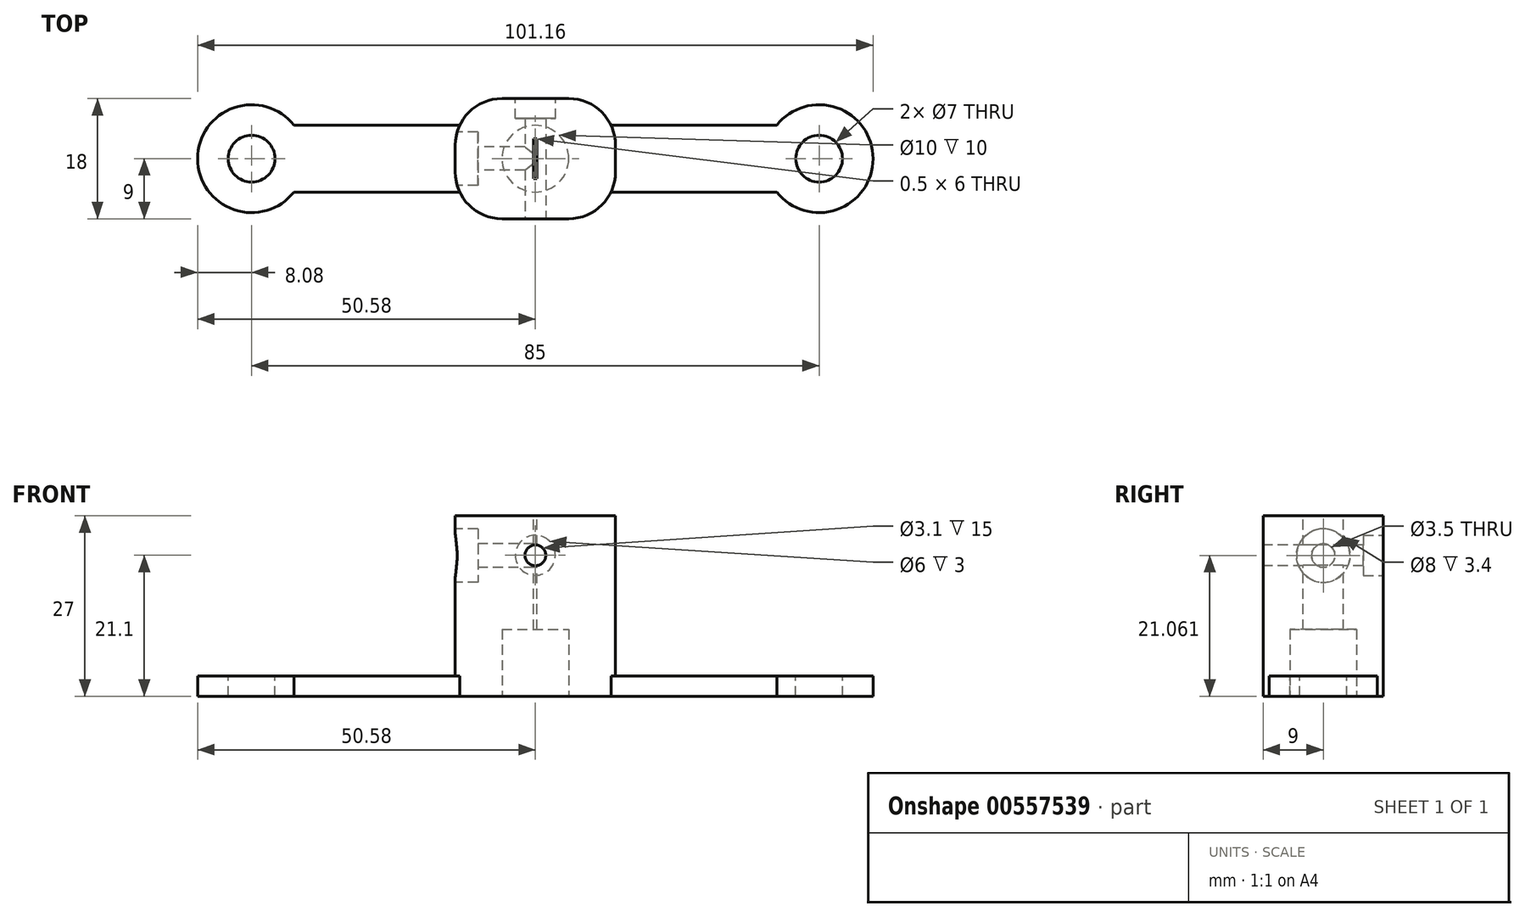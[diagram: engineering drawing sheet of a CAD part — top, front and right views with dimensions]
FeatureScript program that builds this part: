
annotation { "Feature Type Name" : "Feature", "Feature Type Description" : "" }
export const myFeature = defineFeature(function(context is Context, id is Id, definition is map)
    precondition{}
    {
        {
            var Q0;
            Q0=qCreatedBy(makeId("Top.planeOp"),FACE);
            var sketch = newSketch(context, id + "F0", { "sketchPlane" : qUnion([Q0])});
            skLineSegment(sketch, "E0.bottom", {"start": v(42.5, -5) * mm, "end": v(-42.5, -5) * mm});
            skLineSegment(sketch, "E0.top", {"start": v(42.5, 5) * mm, "end": v(-42.5, 5) * mm});
            skLineSegment(sketch, "E0.left", {"start": v(42.5, -5) * mm, "end": v(42.5, 5) * mm});
            skLineSegment(sketch, "E0.right", {"start": v(-42.5, -5) * mm, "end": v(-42.5, 5) * mm});
            skPoint(sketch, "E0.middle", {"position": v(0, 0) * mm});
            skCircle(sketch, "E1", {"center": v(-42.5, 0) * mm, "radius": 8.08 * mm});
            skCircle(sketch, "E2.MirrorC", {"center": v(42.5, 0) * mm, "radius": 8.08 * mm});
            skSolve(sketch);
        }
        {
            var Q0;
            {var subQ0=sQuery(id+"F0.wireOp",EDGE,"E0.left");Q0=makeQuery(id+"F0.imprint","IMPRINT",FACE,{"disambiguationData":[TD([[makeQuery(id+"F0.imprint","IMPRINT",EDGE,{"derivedFrom":subQ0}),-1.0]])]});}
            var Q1;
            {var subQ0=sQuery(id+"F0.wireOp",EDGE,"E0.right");Q1=makeQuery(id+"F0.imprint","IMPRINT",FACE,{"disambiguationData":[TD([[makeQuery(id+"F0.imprint","IMPRINT",EDGE,{"derivedFrom":subQ0}),1.0]])]});}
            var Q2;
            {var subQ0=sQuery(id+"F0.wireOp",EDGE,"E0.left");Q2=makeQuery(id+"F0.imprint","IMPRINT",FACE,{"disambiguationData":[TD([[makeQuery(id+"F0.imprint","IMPRINT",EDGE,{"derivedFrom":subQ0}),1.0]])]});}
            var Q3;
            {var subQ0=sQuery(id+"F0.wireOp",EDGE,"E2.MirrorC");var subQ1=sQuery(id+"F0.wireOp",EDGE,"E0.bottom");var subQ2=makeQuery(id+"F0.imprint","INTERSECT",VERTEX,{"derivedFrom":[subQ1,subQ0]});Q3=makeQuery(id+"F0.imprint","IMPRINT",FACE,{"disambiguationData":[TD([[makeQuery(id+"F0.imprint","IMPRINT",EDGE,{"disambiguationData":[TD([[subQ2,-1.0]])],"derivedFrom":subQ1}),-1.0]])]});}
            var Q4;
            {var subQ0=sQuery(id+"F0.wireOp",EDGE,"E0.right");Q4=makeQuery(id+"F0.imprint","IMPRINT",FACE,{"disambiguationData":[TD([[makeQuery(id+"F0.imprint","IMPRINT",EDGE,{"derivedFrom":subQ0}),-1.0]])]});}
            extrude(context, id + "F1", {"entities" : qUnion([Q0, Q1, Q2, Q3, Q4]), "depth" : 3 * mm, "offsetDistance" : 25 * mm});
        }
        {
            var Q0;
            Q0=makeQuery(id+"F1.opExtrude","CAP_FACE",FACE,{"disambiguationData":[OSD([sQuery(id+"F0.wireOp",EDGE,"E0.bottom"),sQuery(id+"F0.wireOp",EDGE,"E0.top"),sQuery(id+"F0.wireOp",EDGE,"E1"),sQuery(id+"F0.wireOp",EDGE,"E2.MirrorC")])],"isStart":false});
            var sketch = newSketch(context, id + "F2", { "sketchPlane" : qUnion([Q0])});
            skCircle(sketch, "E3", {"center": v(-42.5, 0) * mm, "radius": 3.05 * mm});
            skCircle(sketch, "E4.MirrorC", {"center": v(42.5, 0) * mm, "radius": 3.05 * mm});
            skSolve(sketch);
        }
        {
            var Q0;
            Q0=sQuery(id+"F2.wireOp",VERTEX,"E3.center");
            var Q1;
            Q1=sQuery(id+"F2.wireOp",VERTEX,"E4.MirrorC.center");
            var Q2;
            Q2=makeQuery(id+"F1.opExtrude","SWEPT_BODY",BODY,{"disambiguationData":[OSD([sQuery(id+"F0.wireOp",EDGE,"E0.bottom"),sQuery(id+"F0.wireOp",EDGE,"E0.top"),sQuery(id+"F0.wireOp",EDGE,"E1"),sQuery(id+"F0.wireOp",EDGE,"E2.MirrorC")])]});
            hole(context, id + "F3", {"style" : HoleStyle.SIMPLE, "endStyle" : HoleEndStyle.THROUGH, "holeDiameter" : 7 * mm, "isTappedThrough" : true, "tappedDepth" : 12 * mm, "tapClearance" : 3, "locations" : qUnion([Q0, Q1]), "scope" : qUnion([Q2])});
        }
        {
            var Q0;
            Q0=qCreatedBy(makeId("Top.planeOp"),FACE);
            var sketch = newSketch(context, id + "F4", { "sketchPlane" : qUnion([Q0])});
            skLineSegment(sketch, "E5.bottom", {"start": v(12, 9) * mm, "end": v(-12, 9) * mm});
            skLineSegment(sketch, "E5.top", {"start": v(12, -9) * mm, "end": v(-12, -9) * mm});
            skLineSegment(sketch, "E5.left", {"start": v(12, 9) * mm, "end": v(12, -9) * mm});
            skLineSegment(sketch, "E5.right", {"start": v(-12, 9) * mm, "end": v(-12, -9) * mm});
            skPoint(sketch, "E5.middle", {"position": v(0, 0) * mm});
            skSolve(sketch);
        }
        {
            var Q0;
            Q0=qSketchRegion(id+"F4",true);
            extrude(context, id + "F5", {"entities" : qUnion([Q0]), "operationType" : NewBodyOperationType.ADD, "depth" : 27 * mm, "offsetDistance" : 25 * mm});
        }
        {
            var Q0;
            Q0=qCreatedBy(makeId("Front.planeOp"),FACE);
            var sketch = newSketch(context, id + "F6", { "sketchPlane" : qUnion([Q0])});
            skCircle(sketch, "E6", {"center": v(0, 21.1) * mm, "radius": 1.55 * mm});
            skSolve(sketch);
        }
        {
            var Q0;
            Q0=qSketchRegion(id+"F6",true);
            extrude(context, id + "F7", {"entities" : qUnion([Q0]), "operationType" : NewBodyOperationType.REMOVE, "endBound" : BoundingType.SYMMETRIC, "oppositeDirection" : true, "depth" : 25 * mm, "offsetDistance" : 25 * mm});
        }
        {
            var Q0;
            Q0=makeQuery(id+"F5.opExtrude","SWEPT_FACE",FACE,{"disambiguationData":[OSD([sQuery(id+"F4.wireOp",EDGE,"E5.right")])]});
            var sketch = newSketch(context, id + "F8", { "sketchPlane" : qUnion([Q0])});
            skCircle(sketch, "E7", {"center": v(0, 21.06) * mm, "radius": 1.75 * mm});
            skSolve(sketch);
        }
        {
            var Q0;
            Q0=qSketchRegion(id+"F8",true);
            extrude(context, id + "F9", {"entities" : qUnion([Q0]), "operationType" : NewBodyOperationType.REMOVE, "oppositeDirection" : true, "depth" : 12 * mm, "offsetDistance" : 25 * mm});
        }
        {
            var Q0;
            Q0=makeQuery(id+"F5.opExtrude","SWEPT_FACE",FACE,{"disambiguationData":[OSD([sQuery(id+"F4.wireOp",EDGE,"E5.right")])]});
            var sketch = newSketch(context, id + "F10", { "sketchPlane" : qUnion([Q0])});
            skCircle(sketch, "E8", {"center": v(0, 21.06) * mm, "radius": 4 * mm});
            skSolve(sketch);
        }
        {
            var Q0;
            Q0=qSketchRegion(id+"F10",true);
            extrude(context, id + "F11", {"entities" : qUnion([Q0]), "operationType" : NewBodyOperationType.REMOVE, "oppositeDirection" : true, "depth" : 3.4 * mm, "offsetDistance" : 25 * mm});
        }
        {
            var Q0;
            Q0=makeQuery(id+"F5.opExtrude","SWEPT_EDGE",EDGE,{"disambiguationData":[OSD([sQuery(id+"F4.wireOp",EDGE,"E5.bottom"),sQuery(id+"F4.wireOp",EDGE,"E5.right")])]});
            fillet(context, id + "F12", {"entities" : qUnion([Q0]), "radius" : 7 * mm, "tangentPropagation" : true, "allowEdgeOverflow" : false});
        }
        {
            var Q0;
            Q0=makeQuery(id+"F5.opExtrude","SWEPT_EDGE",EDGE,{"disambiguationData":[OSD([sQuery(id+"F4.wireOp",EDGE,"E5.bottom"),sQuery(id+"F4.wireOp",EDGE,"E5.left")])]});
            fillet(context, id + "F13", {"entities" : qUnion([Q0]), "radius" : 7 * mm, "tangentPropagation" : true, "allowEdgeOverflow" : false});
        }
        {
            var Q0;
            Q0=makeQuery(id+"F5.opExtrude","SWEPT_EDGE",EDGE,{"disambiguationData":[OSD([sQuery(id+"F4.wireOp",EDGE,"E5.top"),sQuery(id+"F4.wireOp",EDGE,"E5.right")])]});
            fillet(context, id + "F14", {"entities" : qUnion([Q0]), "radius" : 7 * mm, "tangentPropagation" : true, "allowEdgeOverflow" : false});
        }
        {
            var Q0;
            Q0=makeQuery(id+"F5.opExtrude","SWEPT_EDGE",EDGE,{"disambiguationData":[OSD([sQuery(id+"F4.wireOp",EDGE,"E5.top"),sQuery(id+"F4.wireOp",EDGE,"E5.left")])]});
            fillet(context, id + "F15", {"entities" : qUnion([Q0]), "radius" : 7 * mm, "tangentPropagation" : true, "allowEdgeOverflow" : false});
        }
        {
            var Q0;
            Q0=makeQuery(id+"F5.opExtrude","CAP_FACE",FACE,{"disambiguationData":[OSD([sQuery(id+"F4.wireOp",EDGE,"E5.bottom"),sQuery(id+"F4.wireOp",EDGE,"E5.top"),sQuery(id+"F4.wireOp",EDGE,"E5.left"),sQuery(id+"F4.wireOp",EDGE,"E5.right")])],"isStart":false});
            var sketch = newSketch(context, id + "F16", { "sketchPlane" : qUnion([Q0])});
            skLineSegment(sketch, "E9.bottom", {"start": v(-0.25, 3) * mm, "end": v(0.25, 3) * mm});
            skLineSegment(sketch, "E9.top", {"start": v(-0.25, -3) * mm, "end": v(0.25, -3) * mm});
            skLineSegment(sketch, "E9.left", {"start": v(-0.25, 3) * mm, "end": v(-0.25, -3) * mm});
            skLineSegment(sketch, "E9.right", {"start": v(0.25, 3) * mm, "end": v(0.25, -3) * mm});
            skPoint(sketch, "E9.middle", {"position": v(0, 0) * mm});
            skSolve(sketch);
        }
        {
            var Q0;
            Q0=qSketchRegion(id+"F16",true);
            extrude(context, id + "F17", {"entities" : qUnion([Q0]), "operationType" : NewBodyOperationType.REMOVE, "oppositeDirection" : true, "depth" : 20 * mm, "offsetDistance" : 25 * mm});
        }
        {
            var Q0;
            Q0=makeQuery(id+"F5.boolean.opBoolean","MERGE",FACE,{"derivedFrom":[makeQuery(id+"F1.opExtrude","CAP_FACE",FACE,{"disambiguationData":[OSD([sQuery(id+"F0.wireOp",EDGE,"E0.bottom"),sQuery(id+"F0.wireOp",EDGE,"E0.top"),sQuery(id+"F0.wireOp",EDGE,"E1"),sQuery(id+"F0.wireOp",EDGE,"E2.MirrorC")])],"isStart":true}),makeQuery(id+"F5.opExtrude","CAP_FACE",FACE,{"disambiguationData":[OSD([sQuery(id+"F4.wireOp",EDGE,"E5.bottom"),sQuery(id+"F4.wireOp",EDGE,"E5.top"),sQuery(id+"F4.wireOp",EDGE,"E5.left"),sQuery(id+"F4.wireOp",EDGE,"E5.right")])],"isStart":true})]});
            var sketch = newSketch(context, id + "F18", { "sketchPlane" : qUnion([Q0])});
            skCircle(sketch, "E10", {"center": v(0, 0) * mm, "radius": 5 * mm});
            skSolve(sketch);
        }
        {
            var Q0;
            Q0=qSketchRegion(id+"F18",true);
            extrude(context, id + "F19", {"entities" : qUnion([Q0]), "operationType" : NewBodyOperationType.REMOVE, "oppositeDirection" : true, "depth" : 10 * mm, "offsetDistance" : 25 * mm});
        }
        {
            var Q0;
            Q0=makeQuery(id+"F5.opExtrude","SWEPT_FACE",FACE,{"disambiguationData":[OSD([sQuery(id+"F4.wireOp",EDGE,"E5.bottom")])]});
            var sketch = newSketch(context, id + "F20", { "sketchPlane" : qUnion([Q0])});
            skCircle(sketch, "E11", {"center": v(0, 21.1) * mm, "radius": 3 * mm});
            skSolve(sketch);
        }
        {
            var Q0;
            Q0=makeQuery(id+"F20.imprint","IMPRINT",FACE,{"disambiguationData":[TD([[makeQuery(id+"F20.imprint","IMPRINT",EDGE,{"derivedFrom":sQuery(id+"F20.wireOp",EDGE,"E11")}),1.0]])]});
            var Q1;
            Q1=sQuery(id+"F20.wireOp",EDGE,"E11");
            extrude(context, id + "F21", {"entities" : qUnion([Q0]), "operationType" : NewBodyOperationType.REMOVE, "surfaceEntities" : qUnion([Q1]), "oppositeDirection" : true, "depth" : 3 * mm, "offsetDistance" : 25 * mm});
        }
    });
